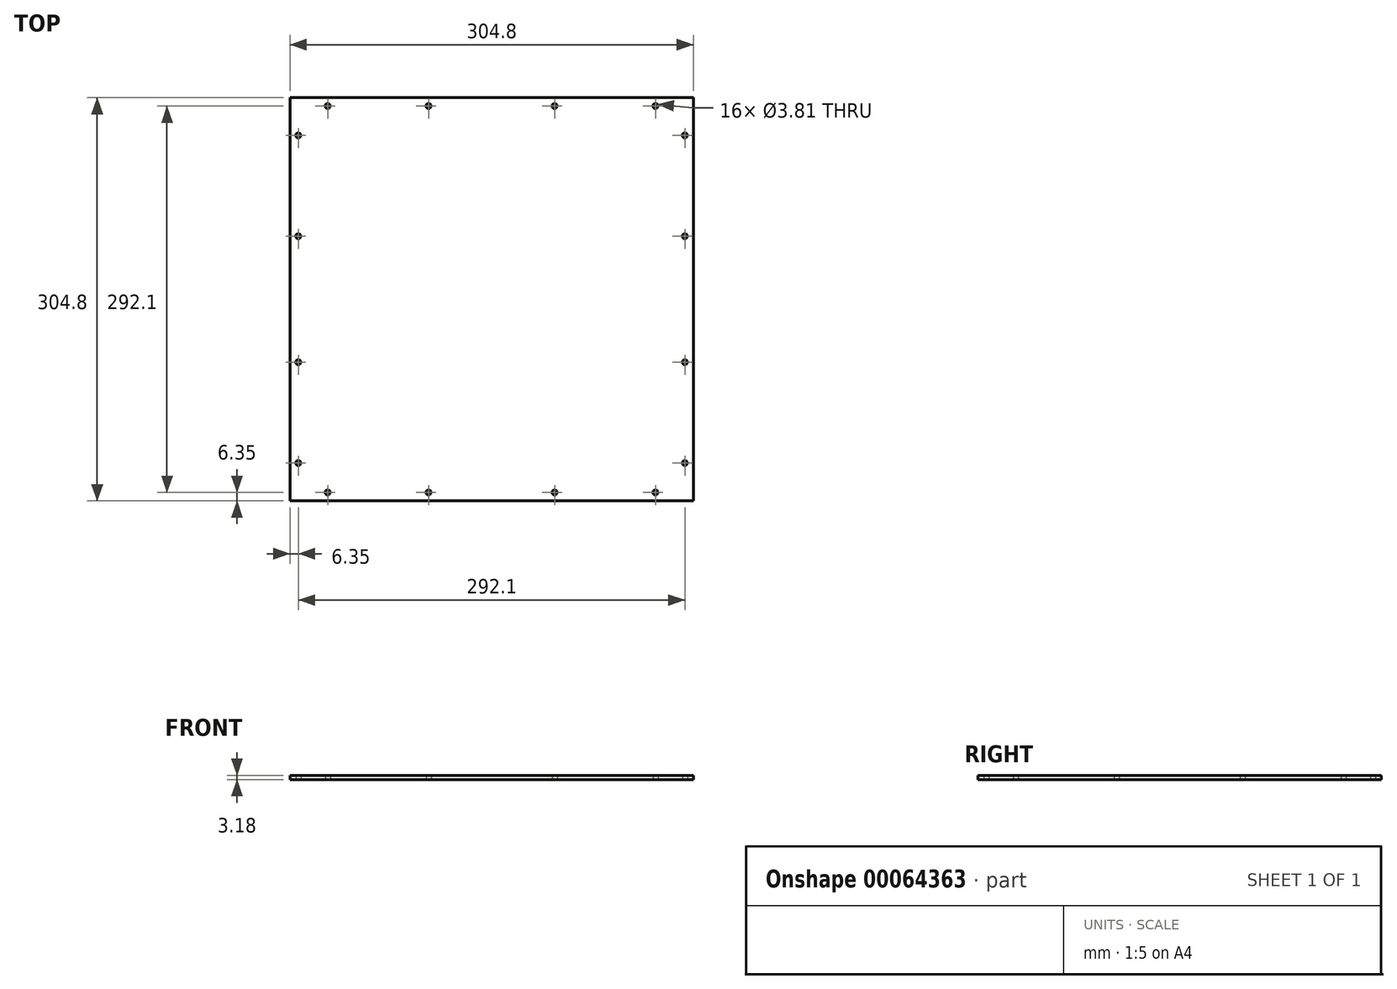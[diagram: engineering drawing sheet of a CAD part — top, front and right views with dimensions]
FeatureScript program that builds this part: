
annotation { "Feature Type Name" : "Feature", "Feature Type Description" : "" }
export const myFeature = defineFeature(function(context is Context, id is Id, definition is map)
    precondition{}
    {
        {
            var Q0;
            Q0=qCreatedBy(makeId("Top.planeOp"),FACE);
            var sketch = newSketch(context, id + "F0", { "sketchPlane" : qUnion([Q0])});
            skLineSegment(sketch, "E0.rect.bottom", {"start": v(-152.4, 152.4) * mm, "end": v(152.4, 152.4) * mm});
            skLineSegment(sketch, "E0.rect.top", {"start": v(-152.4, -152.4) * mm, "end": v(152.4, -152.4) * mm});
            skLineSegment(sketch, "E0.rect.left", {"start": v(-152.4, 152.4) * mm, "end": v(-152.4, -152.4) * mm});
            skLineSegment(sketch, "E0.rect.right", {"start": v(152.4, 152.4) * mm, "end": v(152.4, -152.4) * mm});
            skPoint(sketch, "E1", {"position": v(-47.62, 146.05) * mm});
            skPoint(sketch, "E2", {"position": v(47.63, 146.05) * mm});
            skPoint(sketch, "E3", {"position": v(-47.62, -146.05) * mm});
            skPoint(sketch, "E4", {"position": v(47.63, -146.05) * mm});
            skPoint(sketch, "E5", {"position": v(-146.05, 47.63) * mm});
            skPoint(sketch, "E6", {"position": v(-146.05, -47.62) * mm});
            skPoint(sketch, "E7", {"position": v(146.05, 47.63) * mm});
            skPoint(sketch, "E8", {"position": v(-123.83, 146.05) * mm});
            skPoint(sketch, "E9", {"position": v(-146.05, 123.83) * mm});
            skPoint(sketch, "E10", {"position": v(123.83, 146.05) * mm});
            skPoint(sketch, "E11", {"position": v(-146.05, -123.82) * mm});
            skPoint(sketch, "E12", {"position": v(-123.83, -146.05) * mm});
            skPoint(sketch, "E13", {"position": v(123.83, -146.05) * mm});
            skPoint(sketch, "E14", {"position": v(146.05, -123.82) * mm});
            skPoint(sketch, "E15", {"position": v(146.05, 123.83) * mm});
            skPoint(sketch, "E16", {"position": v(146.05, -47.62) * mm});
            skPoint(sketch, "E17.rect.middle", {"position": v(0, 0) * mm});
            skSolve(sketch);
        }
        {
            var Q0;
            Q0=qSketchRegion(id+"F0",true);
            extrude(context, id + "F1", {"entities" : qUnion([Q0]), "depth" : 3.17 * mm});
        }
        {
            var Q0;
            Q0=sQuery(id+"F0.wireOp",VERTEX,"E9");
            var Q1;
            Q1=sQuery(id+"F0.wireOp",VERTEX,"E8");
            var Q2;
            Q2=sQuery(id+"F0.wireOp",VERTEX,"E10");
            var Q3;
            Q3=sQuery(id+"F0.wireOp",VERTEX,"E14");
            var Q4;
            Q4=sQuery(id+"F0.wireOp",VERTEX,"E13");
            var Q5;
            Q5=sQuery(id+"F0.wireOp",VERTEX,"E11");
            var Q6;
            Q6=sQuery(id+"F0.wireOp",VERTEX,"E12");
            var Q7;
            Q7=sQuery(id+"F0.wireOp",VERTEX,"E5");
            var Q8;
            Q8=sQuery(id+"F0.wireOp",VERTEX,"E6");
            var Q9;
            Q9=sQuery(id+"F0.wireOp",VERTEX,"E3");
            var Q10;
            Q10=sQuery(id+"F0.wireOp",VERTEX,"E4");
            var Q11;
            Q11=sQuery(id+"F0.wireOp",VERTEX,"E16");
            var Q12;
            Q12=sQuery(id+"F0.wireOp",VERTEX,"E7");
            var Q13;
            Q13=sQuery(id+"F0.wireOp",VERTEX,"E2");
            var Q14;
            Q14=sQuery(id+"F0.wireOp",VERTEX,"E1");
            var Q15;
            Q15=sQuery(id+"F0.wireOp",VERTEX,"E15");
            var Q16;
            Q16=makeQuery(id+"F1.opExtrude","SWEPT_BODY",BODY,{"disambiguationData":[OSD([sQuery(id+"F0.wireOp",EDGE,"E0.rect.bottom"),sQuery(id+"F0.wireOp",EDGE,"E0.rect.top"),sQuery(id+"F0.wireOp",EDGE,"E0.rect.left"),sQuery(id+"F0.wireOp",EDGE,"E0.rect.right"),sQuery(id+"F0.wireOp",EDGE,"355e2ae6-6e88-4ca4-8ebc-3fd0fd05b8a7"),sQuery(id+"F0.wireOp",EDGE,"ec92c217-216e-4417-a66e-f22207dcd941.0.1.0"),sQuery(id+"F0.wireOp",EDGE,"ec92c217-216e-4417-a66e-f22207dcd941.1.0.0"),sQuery(id+"F0.wireOp",EDGE,"ec92c217-216e-4417-a66e-f22207dcd941.1.1.0"),sQuery(id+"F0.wireOp",EDGE,"73b4038f-2a48-4c89-9a6c-eaebf8faa2ab.0.1.4"),sQuery(id+"F0.wireOp",EDGE,"73b4038f-2a48-4c89-9a6c-eaebf8faa2ab.0.1.5"),sQuery(id+"F0.wireOp",EDGE,"73b4038f-2a48-4c89-9a6c-eaebf8faa2ab.0.1.6"),sQuery(id+"F0.wireOp",EDGE,"73b4038f-2a48-4c89-9a6c-eaebf8faa2ab.0.1.7"),sQuery(id+"F0.wireOp",EDGE,"73b4038f-2a48-4c89-9a6c-eaebf8faa2ab.0.2.4"),sQuery(id+"F0.wireOp",EDGE,"73b4038f-2a48-4c89-9a6c-eaebf8faa2ab.0.2.5"),sQuery(id+"F0.wireOp",EDGE,"73b4038f-2a48-4c89-9a6c-eaebf8faa2ab.0.2.6"),sQuery(id+"F0.wireOp",EDGE,"73b4038f-2a48-4c89-9a6c-eaebf8faa2ab.0.2.7"),sQuery(id+"F0.wireOp",EDGE,"73b4038f-2a48-4c89-9a6c-eaebf8faa2ab.1.0.4"),sQuery(id+"F0.wireOp",EDGE,"73b4038f-2a48-4c89-9a6c-eaebf8faa2ab.1.0.5"),sQuery(id+"F0.wireOp",EDGE,"73b4038f-2a48-4c89-9a6c-eaebf8faa2ab.1.0.6"),sQuery(id+"F0.wireOp",EDGE,"73b4038f-2a48-4c89-9a6c-eaebf8faa2ab.1.0.7"),sQuery(id+"F0.wireOp",EDGE,"73b4038f-2a48-4c89-9a6c-eaebf8faa2ab.1.1.4"),sQuery(id+"F0.wireOp",EDGE,"73b4038f-2a48-4c89-9a6c-eaebf8faa2ab.1.1.5"),sQuery(id+"F0.wireOp",EDGE,"73b4038f-2a48-4c89-9a6c-eaebf8faa2ab.1.1.6"),sQuery(id+"F0.wireOp",EDGE,"73b4038f-2a48-4c89-9a6c-eaebf8faa2ab.1.1.7"),sQuery(id+"F0.wireOp",EDGE,"73b4038f-2a48-4c89-9a6c-eaebf8faa2ab.1.2.4"),sQuery(id+"F0.wireOp",EDGE,"73b4038f-2a48-4c89-9a6c-eaebf8faa2ab.1.2.5"),sQuery(id+"F0.wireOp",EDGE,"73b4038f-2a48-4c89-9a6c-eaebf8faa2ab.1.2.6"),sQuery(id+"F0.wireOp",EDGE,"73b4038f-2a48-4c89-9a6c-eaebf8faa2ab.1.2.7"),sQuery(id+"F0.wireOp",EDGE,"73b4038f-2a48-4c89-9a6c-eaebf8faa2ab.2.0.4"),sQuery(id+"F0.wireOp",EDGE,"73b4038f-2a48-4c89-9a6c-eaebf8faa2ab.2.0.5"),sQuery(id+"F0.wireOp",EDGE,"73b4038f-2a48-4c89-9a6c-eaebf8faa2ab.2.0.6"),sQuery(id+"F0.wireOp",EDGE,"73b4038f-2a48-4c89-9a6c-eaebf8faa2ab.2.0.7"),sQuery(id+"F0.wireOp",EDGE,"73b4038f-2a48-4c89-9a6c-eaebf8faa2ab.2.1.4"),sQuery(id+"F0.wireOp",EDGE,"73b4038f-2a48-4c89-9a6c-eaebf8faa2ab.2.1.5"),sQuery(id+"F0.wireOp",EDGE,"73b4038f-2a48-4c89-9a6c-eaebf8faa2ab.2.1.6"),sQuery(id+"F0.wireOp",EDGE,"73b4038f-2a48-4c89-9a6c-eaebf8faa2ab.2.1.7"),sQuery(id+"F0.wireOp",EDGE,"73b4038f-2a48-4c89-9a6c-eaebf8faa2ab.2.2.4"),sQuery(id+"F0.wireOp",EDGE,"73b4038f-2a48-4c89-9a6c-eaebf8faa2ab.2.2.5"),sQuery(id+"F0.wireOp",EDGE,"73b4038f-2a48-4c89-9a6c-eaebf8faa2ab.2.2.6"),sQuery(id+"F0.wireOp",EDGE,"73b4038f-2a48-4c89-9a6c-eaebf8faa2ab.2.2.7"),sQuery(id+"F0.wireOp",EDGE,"afade619-a39a-4778-b8e1-03a779a9a28b"),sQuery(id+"F0.wireOp",EDGE,"8a805056-4bb3-49c9-a1bc-3d3538aac092.0.1.0"),sQuery(id+"F0.wireOp",EDGE,"8a805056-4bb3-49c9-a1bc-3d3538aac092.0.2.0"),sQuery(id+"F0.wireOp",EDGE,"8a805056-4bb3-49c9-a1bc-3d3538aac092.1.0.0"),sQuery(id+"F0.wireOp",EDGE,"8a805056-4bb3-49c9-a1bc-3d3538aac092.1.1.0"),sQuery(id+"F0.wireOp",EDGE,"8a805056-4bb3-49c9-a1bc-3d3538aac092.1.2.0"),sQuery(id+"F0.wireOp",EDGE,"8a805056-4bb3-49c9-a1bc-3d3538aac092.2.0.0"),sQuery(id+"F0.wireOp",EDGE,"8a805056-4bb3-49c9-a1bc-3d3538aac092.2.1.0"),sQuery(id+"F0.wireOp",EDGE,"8a805056-4bb3-49c9-a1bc-3d3538aac092.2.2.0")])]});
            hole(context, id + "F2", {"style" : HoleStyle.SIMPLE, "holeDiameter" : 3.8 * mm, "endStyle" : HoleEndStyle.THROUGH, "oppositeDirection" : true, "locations" : qUnion([Q0, Q1, Q2, Q3, Q4, Q5, Q6, Q7, Q8, Q9, Q10, Q11, Q12, Q13, Q14, Q15]), "scope" : qUnion([Q16])});
        }
    });
